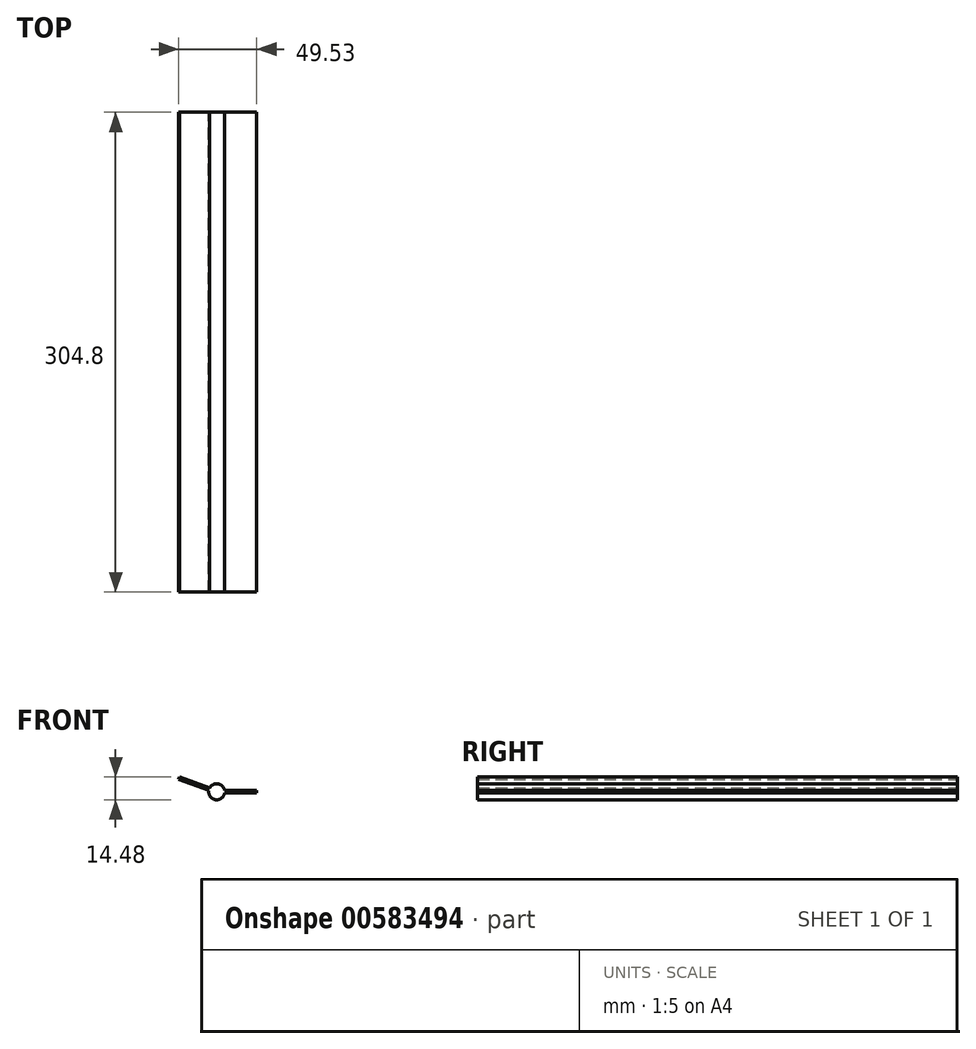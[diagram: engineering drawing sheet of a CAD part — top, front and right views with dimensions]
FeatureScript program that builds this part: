
annotation { "Feature Type Name" : "Feature", "Feature Type Description" : "" }
export const myFeature = defineFeature(function(context is Context, id is Id, definition is map)
    precondition{}
    {
        {
            var Q0;
            Q0=qCreatedBy(makeId("Front.planeOp"),FACE);
            var sketch = newSketch(context, id + "F0", { "sketchPlane" : qUnion([Q0])});
            skArc(sketch, "E0", {"start": v(-4.98, 1) * mm, "mid": v(-0.88, -5) * mm, "end": v(5.02, -0.76) * mm});
            skLineSegment(sketch, "E1", {"start": v(25.4, -0.76) * mm, "end": v(25.4, 0.76) * mm});
            skLineSegment(sketch, "E2", {"start": v(25.4, 0.76) * mm, "end": v(5.02, 0.76) * mm});
            skLineSegment(sketch, "E3", {"start": v(25.4, -0.76) * mm, "end": v(5.02, -0.76) * mm});
            skLineSegment(sketch, "E4", {"start": v(0, 0) * mm, "end": v(-23.87, 8.69) * mm, "construction": true});
            skLineSegment(sketch, "E5", {"start": v(-23.87, 8.69) * mm, "end": v(-23.6, 9.4) * mm});
            skLineSegment(sketch, "E6", {"start": v(-23.87, 8.69) * mm, "end": v(-24.13, 7.97) * mm});
            skLineSegment(sketch, "E7", {"start": v(-24.13, 7.97) * mm, "end": v(-4.98, 1) * mm});
            skLineSegment(sketch, "E8", {"start": v(-23.6, 9.4) * mm, "end": v(-4.46, 2.43) * mm});
            skArc(sketch, "E9.trimOffspring", {"start": v(5.02, 0.76) * mm, "mid": v(0.88, 5) * mm, "end": v(-4.46, 2.43) * mm});
            skSolve(sketch);
        }
        {
            var Q0;
            Q0=makeQuery(id+"F0.imprint","IMPRINT",FACE,{"disambiguationData":[TD([[makeQuery(id+"F0.imprint","IMPRINT",EDGE,{"derivedFrom":sQuery(id+"F0.wireOp",EDGE,"E0")}),1.0]])]});
            extrude(context, id + "F1", {"entities" : qUnion([Q0]), "depth" : 304.8 * mm, "offsetDistance" : 25.4 * mm});
        }
    });
